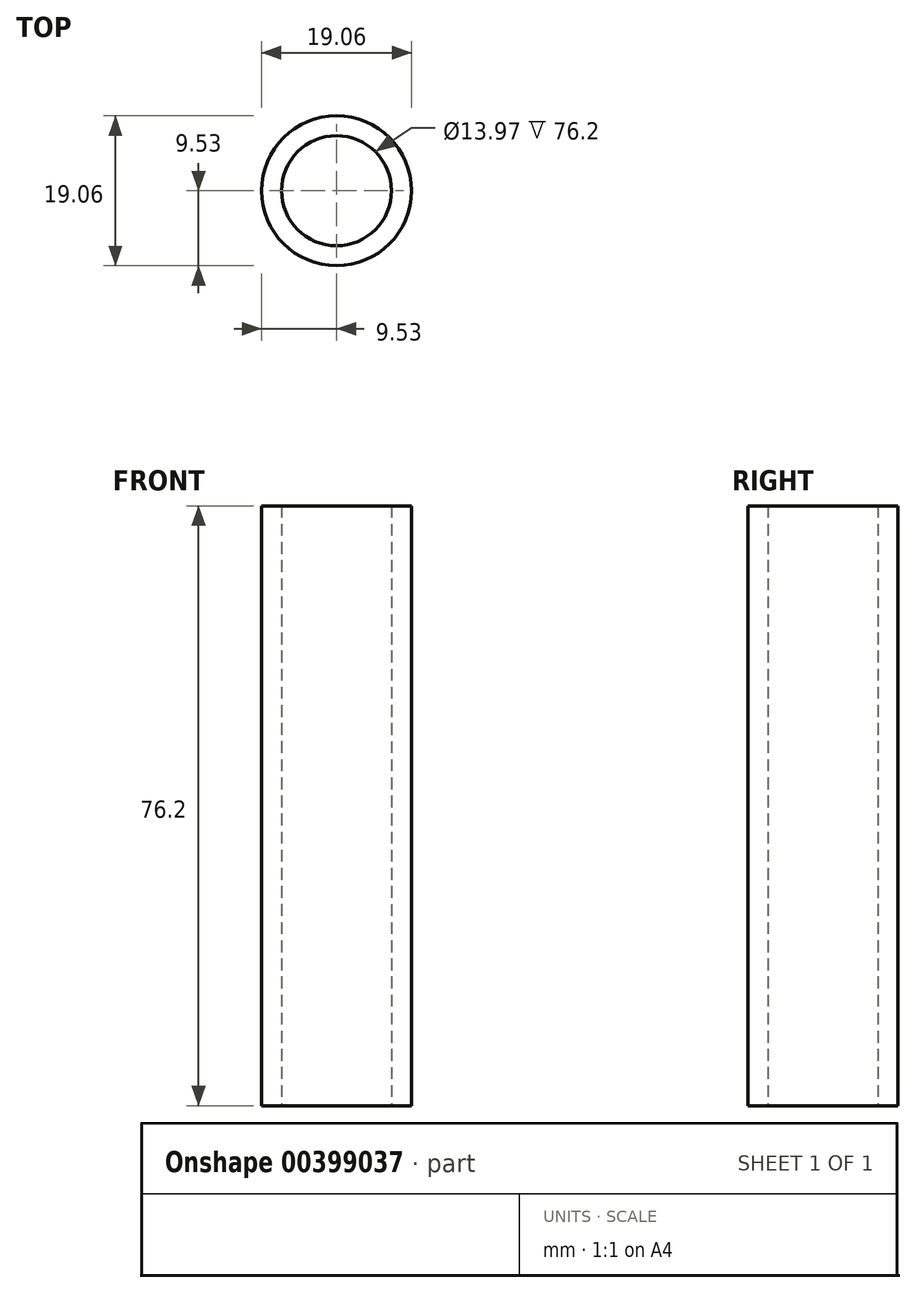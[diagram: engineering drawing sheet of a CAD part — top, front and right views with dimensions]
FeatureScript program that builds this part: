
annotation { "Feature Type Name" : "Feature", "Feature Type Description" : "" }
export const myFeature = defineFeature(function(context is Context, id is Id, definition is map)
    precondition{}
    {
        {
            var Q0;
            Q0=qCreatedBy(makeId("Top.planeOp"),FACE);
            var sketch = newSketch(context, id + "F0", { "sketchPlane" : qUnion([Q0])});
            skCircle(sketch, "E0", {"center": v(0, 0) * mm, "radius": 9.53 * mm});
            skSolve(sketch);
        }
        {
            var Q0;
            Q0 = qSketchRegion(id + "F0", true);
            extrude(context, id + "F1", {"entities" : qUnion([Q0]), "depth" : 76.2 * mm, "symmetric" : true});
        }
        {
            var Q0;
            Q0=makeQuery(id+"F1.opExtrude","CAP_FACE",FACE,{"disambiguationData":[OSD([sQuery(id+"F0.wireOp",EDGE,"E0")])],"isStart":false});
            var Q1;
            Q1=makeQuery(id+"F1.opExtrude","CAP_FACE",FACE,{"disambiguationData":[OSD([sQuery(id+"F0.wireOp",EDGE,"E0")])],"isStart":true});
            shell(context, id + "F2", {"entities" : qUnion([Q0, Q1]), "thickness" : 2.54 * mm});
        }
    });
